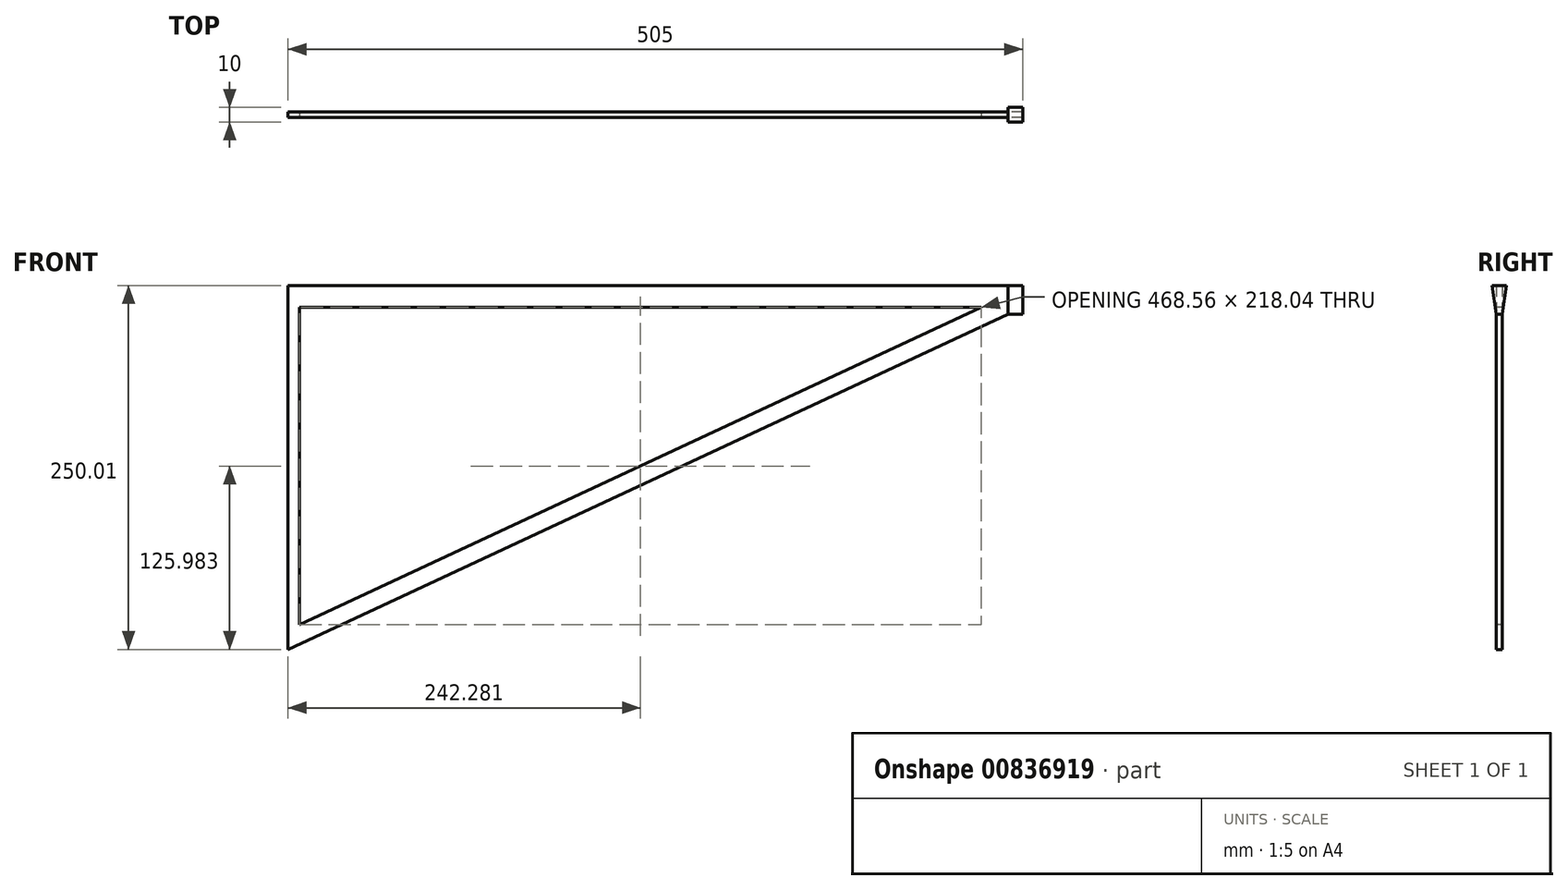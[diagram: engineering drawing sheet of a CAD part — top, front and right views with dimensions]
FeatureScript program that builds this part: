
annotation { "Feature Type Name" : "Feature", "Feature Type Description" : "" }
export const myFeature = defineFeature(function(context is Context, id is Id, definition is map)
    precondition{}
    {
        {
            var Q0;
            Q0=qCreatedBy(makeId("Front.planeOp"),FACE);
            var sketch = newSketch(context, id + "F0", { "sketchPlane" : qUnion([Q0])});
            skLineSegment(sketch, "E0", {"start": v(-265.3, 112.83) * mm, "end": v(239.7, 112.83) * mm});
            skLineSegment(sketch, "E1", {"start": v(239.7, 112.83) * mm, "end": v(239.7, 97.83) * mm});
            skLineSegment(sketch, "E2", {"start": v(239.7, 97.83) * mm, "end": v(-265.3, -137.17) * mm});
            skLineSegment(sketch, "E3", {"start": v(-265.3, 112.83) * mm, "end": v(-265.3, -137.17) * mm});
            skSolve(sketch);
        }
        {
            var Q0;
            Q0=makeQuery(id+"F0.imprint","IMPRINT",FACE,{"disambiguationData":[TD([[makeQuery(id+"F0.imprint","IMPRINT",EDGE,{"derivedFrom":sQuery(id+"F0.wireOp",EDGE,"E0")}),-1.0]])]});
            extrude(context, id + "F1", {"entities" : qUnion([Q0]), "depth" : 4 * mm, "offsetDistance" : 25.4 * mm});
        }
        {
            var Q0;
            Q0=makeQuery(id+"F1.opExtrude","CAP_FACE",FACE,{"disambiguationData":[OSD([sQuery(id+"F0.wireOp",EDGE,"E0"),sQuery(id+"F0.wireOp",EDGE,"ZiBb8iuL-fdfZ-lSes-VR4x-yMFCXHXkicfL"),sQuery(id+"F0.wireOp",EDGE,"nwZBxdzl-NFel-4kml-vlfn-ZsOfbEv7kmnL")])],"isStart":false});
            var sketch = newSketch(context, id + "F2", { "sketchPlane" : qUnion([Q0])});
            skLineSegment(sketch, "E4", {"start": v(189.46, 97.83) * mm, "end": v(-257.3, 97.83) * mm});
            skLineSegment(sketch, "E5", {"start": v(-257.3, 97.83) * mm, "end": v(-257.3, -120.2) * mm});
            skLineSegment(sketch, "E6", {"start": v(-257.3, -120.2) * mm, "end": v(191.92, 88.83) * mm});
            skLineSegment(sketch, "E7", {"start": v(189.46, 97.83) * mm, "end": v(211.26, 97.83) * mm});
            skLineSegment(sketch, "E8", {"start": v(191.92, 88.83) * mm, "end": v(211.26, 97.83) * mm});
            skSolve(sketch);
        }
        {
            var Q0;
            Q0=makeQuery(id+"F2.imprint","IMPRINT",FACE,{"disambiguationData":[TD([[makeQuery(id+"F2.imprint","IMPRINT",EDGE,{"derivedFrom":sQuery(id+"F2.wireOp",EDGE,"E4")}),1.0]])]});
            extrude(context, id + "F3", {"entities" : qUnion([Q0]), "operationType" : NewBodyOperationType.REMOVE, "oppositeDirection" : true, "depth" : 4 * mm, "offsetDistance" : 25.4 * mm});
        }
        {
            var Q0;
            Q0=makeQuery(id+"F1.opExtrude","SWEPT_FACE",FACE,{"disambiguationData":[OSD([sQuery(id+"F0.wireOp",EDGE,"E0")])]});
            var sketch = newSketch(context, id + "F4", { "sketchPlane" : qUnion([Q0])});
            skLineSegment(sketch, "E9.bottom", {"start": v(239.7, 3) * mm, "end": v(229.7, 3) * mm});
            skLineSegment(sketch, "E9.top", {"start": v(239.7, -7) * mm, "end": v(229.7, -7) * mm});
            skLineSegment(sketch, "E9.right", {"start": v(229.7, 3) * mm, "end": v(229.7, -7) * mm});
            skLineSegment(sketch, "E10", {"start": v(239.7, 3) * mm, "end": v(239.7, -7) * mm});
            skSolve(sketch);
        }
        {
            var Q0;
            Q0 = qSketchRegion(id + "F4", true);
            extrude(context, id + "F5", {"entities" : qUnion([Q0]), "operationType" : NewBodyOperationType.ADD, "oppositeDirection" : true, "depth" : 24.8 * mm, "offsetDistance" : 25.4 * mm});
        }
        {
            var Q0;
            Q0=makeQuery(id+"F5.opExtrude","SWEPT_FACE",FACE,{"disambiguationData":[OSD([sQuery(id+"F4.wireOp",EDGE,"E9.right")])]});
            var sketch = newSketch(context, id + "F6", { "sketchPlane" : qUnion([Q0])});
            skLineSegment(sketch, "E11", {"start": v(4, 93.18) * mm, "end": v(7, 112.83) * mm});
            skLineSegment(sketch, "E12", {"start": v(0, 93.18) * mm, "end": v(-3, 112.83) * mm});
            skSolve(sketch);
        }
        {
            var Q0;
            Q0=makeQuery(id+"F6.imprint","IMPRINT",FACE,{"disambiguationData":[TD([[makeQuery(id+"F6.imprint","IMPRINT",EDGE,{"derivedFrom":sQuery(id+"F6.wireOp",EDGE,"E11")}),-1.0]])]});
            extrude(context, id + "F7", {"entities" : qUnion([Q0]), "operationType" : NewBodyOperationType.REMOVE, "oppositeDirection" : true, "depth" : 10 * mm, "offsetDistance" : 25.4 * mm});
        }
        {
            var Q0;
            Q0=makeQuery(id+"F1.opExtrude","CAP_FACE",FACE,{"disambiguationData":[OSD([sQuery(id+"F0.wireOp",EDGE,"E0"),sQuery(id+"F0.wireOp",EDGE,"nwZBxdzl-NFel-4kml-vlfn-ZsOfbEv7kmnL"),sQuery(id+"F0.wireOp",EDGE,"E1"),sQuery(id+"F0.wireOp",EDGE,"E2")])],"isStart":false});
            var sketch = newSketch(context, id + "F8", { "sketchPlane" : qUnion([Q0])});
            skLineSegment(sketch, "E13", {"start": v(241.74, 93.18) * mm, "end": v(-265.3, -137.17) * mm});
            skLineSegment(sketch, "E14", {"start": v(-265.3, -137.17) * mm, "end": v(229.7, 93.18) * mm});
            skLineSegment(sketch, "E15", {"start": v(229.7, 93.18) * mm, "end": v(241.74, 93.18) * mm});
            skSolve(sketch);
        }
        {
            var Q0;
            Q0=makeQuery(id+"F8.imprint","IMPRINT",FACE,{"disambiguationData":[TD([[makeQuery(id+"F8.imprint","IMPRINT",EDGE,{"derivedFrom":sQuery(id+"F8.wireOp",EDGE,"E13")}),-1.0]])]});
            extrude(context, id + "F9", {"entities" : qUnion([Q0]), "oppositeDirection" : true, "depth" : 4 * mm, "offsetDistance" : 25.4 * mm});
        }
        {
            var Q0;
            Q0=makeQuery(id+"F9.opExtrude","SWEPT_BODY",BODY,{"disambiguationData":[OSD([sQuery(id+"F8.wireOp",EDGE,"E13"),sQuery(id+"F8.wireOp",EDGE,"E14"),sQuery(id+"F8.wireOp",EDGE,"E15")])]});
            deleteBodies(context, id + "F10", {"entities" : qUnion([Q0])});
        }
        {
            var Q0;
            {var subQ0=sQuery(id+"F4.wireOp",EDGE,"E9.bottom");Q0=makeQuery(id+"F4.imprint","IMPRINT",FACE,{"disambiguationData":[TD([[makeQuery(id+"F4.imprint","IMPRINT",EDGE,{"derivedFrom":subQ0}),1.0]])]});}
            var Q1;
            {var subQ0=sQuery(id+"F4.wireOp",EDGE,"E9.right");var subQ1=sQuery(id+"F0.wireOp",EDGE,"E0");var subQ2=makeQuery(id+"F1.opExtrude","CAP_EDGE",EDGE,{"disambiguationData":[OSD([subQ1])],"isStart":true});var subQ3=makeQuery(id+"F4.imprint","INTERSECT",VERTEX,{"derivedFrom":[subQ2,subQ0]});Q1=makeQuery(id+"F4.imprint","IMPRINT",FACE,{"disambiguationData":[TD([[makeQuery(id+"F4.imprint","IMPRINT",EDGE,{"disambiguationData":[TD([[subQ3,-1.0]])],"derivedFrom":subQ0}),1.0]])]});}
            var Q2;
            {var subQ0=sQuery(id+"F4.wireOp",EDGE,"E9.top");Q2=makeQuery(id+"F4.imprint","IMPRINT",FACE,{"disambiguationData":[TD([[makeQuery(id+"F4.imprint","IMPRINT",EDGE,{"derivedFrom":subQ0}),-1.0]])]});}
            extrude(context, id + "F11", {"entities" : qUnion([Q0, Q1, Q2]), "operationType" : NewBodyOperationType.ADD, "depth" : 0.01 * mm, "offsetDistance" : 25.4 * mm});
        }
    });
